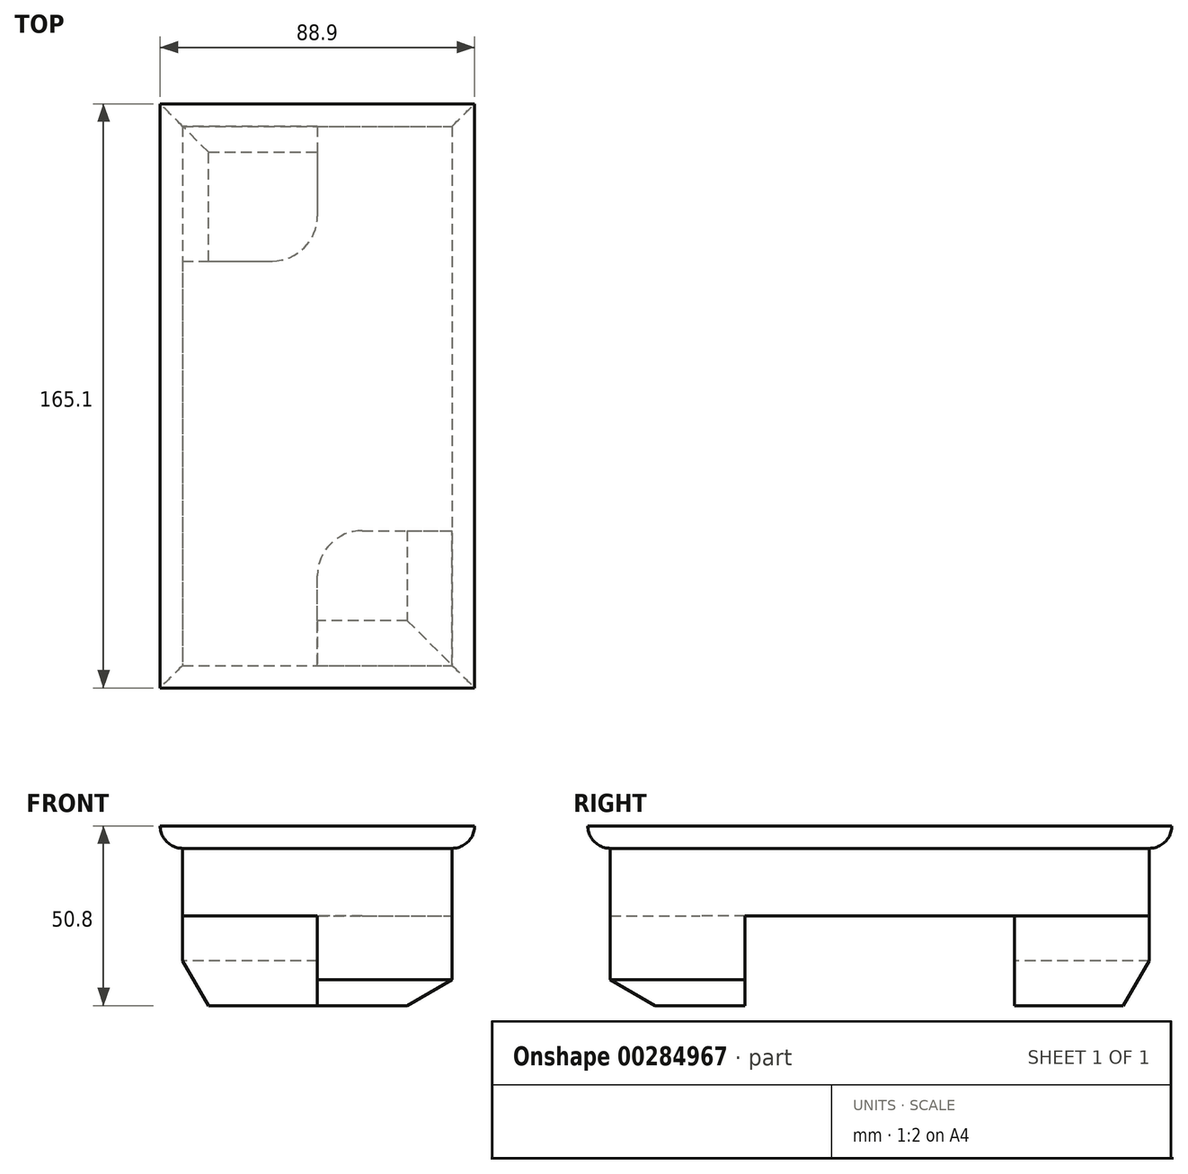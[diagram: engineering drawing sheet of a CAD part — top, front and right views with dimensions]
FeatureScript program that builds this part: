
annotation { "Feature Type Name" : "Feature", "Feature Type Description" : "" }
export const myFeature = defineFeature(function(context is Context, id is Id, definition is map)
    precondition{}
    {
        {
            var Q0;
            Q0=qCreatedBy(makeId("Top.planeOp"),FACE);
            var sketch = newSketch(context, id + "F0", { "sketchPlane" : qUnion([Q0])});
            skLineSegment(sketch, "E0.bottom", {"start": v(-82.55, 51.12) * mm, "end": v(-6.35, 51.12) * mm});
            skLineSegment(sketch, "E0.top", {"start": v(-82.55, -101.28) * mm, "end": v(-6.35, -101.28) * mm});
            skLineSegment(sketch, "E0.left", {"start": v(-82.55, 51.12) * mm, "end": v(-82.55, -101.28) * mm});
            skLineSegment(sketch, "E0.right", {"start": v(-6.35, 51.12) * mm, "end": v(-6.35, -101.28) * mm});
            skLineSegment(sketch, "E1.0", {"start": v(-88.9, 57.47) * mm, "end": v(0, 57.47) * mm});
            skLineSegment(sketch, "E1.1", {"start": v(-88.9, 57.47) * mm, "end": v(-88.9, -107.63) * mm});
            skLineSegment(sketch, "E1.2", {"start": v(-88.9, -107.63) * mm, "end": v(0, -107.63) * mm});
            skLineSegment(sketch, "E1.3", {"start": v(0, 57.47) * mm, "end": v(0, -107.63) * mm});
            skLineSegment(sketch, "E2", {"start": v(-82.55, 13.02) * mm, "end": v(-57.15, 13.02) * mm});
            skLineSegment(sketch, "E3", {"start": v(-44.45, 51.12) * mm, "end": v(-44.45, 25.72) * mm});
            skLineSegment(sketch, "E4", {"start": v(-44.45, -101.28) * mm, "end": v(-44.45, -75.88) * mm});
            skLineSegment(sketch, "E5", {"start": v(-31.75, -63.18) * mm, "end": v(-6.35, -63.18) * mm});
            skPoint(sketch, "E6.visualSharp", {"position": v(-44.45, 13.02) * mm});
            skArc(sketch, "E6.filletArc", {"start": v(-57.15, 13.02) * mm, "mid": v(-48.17, 16.74) * mm, "end": v(-44.45, 25.72) * mm});
            skPoint(sketch, "E7.visualSharp", {"position": v(-44.45, -63.18) * mm});
            skArc(sketch, "E7.filletArc", {"start": v(-31.75, -63.18) * mm, "mid": v(-40.73, -66.9) * mm, "end": v(-44.45, -75.88) * mm});
            skSolve(sketch);
        }
        {
            var Q0;
            Q0=makeQuery(id+"F0.imprint","IMPRINT",FACE,{"disambiguationData":[TD([[makeQuery(id+"F0.imprint","IMPRINT",EDGE,{"derivedFrom":sQuery(id+"F0.wireOp",EDGE,"E1.0")}),-1.0]])]});
            var Q1;
            {var subQ3=sQuery(id+"F0.wireOp",EDGE,"E2");Q1=makeQuery(id+"F0.imprint","IMPRINT",FACE,{"disambiguationData":[TD([[makeQuery(id+"F0.imprint","IMPRINT",EDGE,{"derivedFrom":subQ3}),-1.0]])]});}
            var Q2;
            {var subQ1=sQuery(id+"F0.wireOp",EDGE,"E4");Q2=makeQuery(id+"F0.imprint","IMPRINT",FACE,{"disambiguationData":[TD([[makeQuery(id+"F0.imprint","IMPRINT",EDGE,{"derivedFrom":subQ1}),-1.0]])]});}
            var Q3;
            {var subQ1=sQuery(id+"F0.wireOp",EDGE,"E2");Q3=makeQuery(id+"F0.imprint","IMPRINT",FACE,{"disambiguationData":[TD([[makeQuery(id+"F0.imprint","IMPRINT",EDGE,{"derivedFrom":subQ1}),1.0]])]});}
            extrude(context, id + "F1", {"entities" : qUnion([Q0, Q1, Q2, Q3]), "oppositeDirection" : true, "depth" : 6.35 * mm});
        }
        {
            var Q0;
            {var subQ3=sQuery(id+"F0.wireOp",EDGE,"E2");Q0=makeQuery(id+"F0.imprint","IMPRINT",FACE,{"disambiguationData":[TD([[makeQuery(id+"F0.imprint","IMPRINT",EDGE,{"derivedFrom":subQ3}),-1.0]])]});}
            extrude(context, id + "F2", {"entities" : qUnion([Q0]), "operationType" : NewBodyOperationType.ADD, "oppositeDirection" : true, "depth" : 25.4 * mm});
        }
        {
            var Q0;
            {var subQ1=sQuery(id+"F0.wireOp",EDGE,"E4");Q0=makeQuery(id+"F0.imprint","IMPRINT",FACE,{"disambiguationData":[TD([[makeQuery(id+"F0.imprint","IMPRINT",EDGE,{"derivedFrom":subQ1}),-1.0]])]});}
            var Q1;
            {var subQ1=sQuery(id+"F0.wireOp",EDGE,"E2");Q1=makeQuery(id+"F0.imprint","IMPRINT",FACE,{"disambiguationData":[TD([[makeQuery(id+"F0.imprint","IMPRINT",EDGE,{"derivedFrom":subQ1}),1.0]])]});}
            extrude(context, id + "F3", {"entities" : qUnion([Q0, Q1]), "operationType" : NewBodyOperationType.ADD, "oppositeDirection" : true, "depth" : 50.8 * mm});
        }
        {
            var Q0;
            Q0=makeQuery(id+"F1.opExtrude","CAP_EDGE",EDGE,{"disambiguationData":[OSD([sQuery(id+"F0.wireOp",EDGE,"E1.0")])],"isStart":false});
            var Q1;
            Q1=makeQuery(id+"F1.opExtrude","CAP_EDGE",EDGE,{"disambiguationData":[OSD([sQuery(id+"F0.wireOp",EDGE,"E1.3")])],"isStart":false});
            var Q2;
            Q2=makeQuery(id+"F1.opExtrude","CAP_EDGE",EDGE,{"disambiguationData":[OSD([sQuery(id+"F0.wireOp",EDGE,"E1.2")])],"isStart":false});
            var Q3;
            Q3=makeQuery(id+"F1.opExtrude","CAP_EDGE",EDGE,{"disambiguationData":[OSD([sQuery(id+"F0.wireOp",EDGE,"E1.1")])],"isStart":false});
            fillet(context, id + "F4", {"entities" : qUnion([Q0, Q1, Q2, Q3]), "radius" : 6.35 * mm, "tangentPropagation" : true, "allowEdgeOverflow" : false});
        }
        {
            var Q0;
            Q0=makeQuery(id+"F3.opExtrude","CAP_EDGE",EDGE,{"disambiguationData":[OSD([sQuery(id+"F0.wireOp",EDGE,"E0.right")])],"isStart":false});
            var Q1;
            Q1=makeQuery(id+"F3.opExtrude","CAP_EDGE",EDGE,{"disambiguationData":[OSD([sQuery(id+"F0.wireOp",EDGE,"E0.top")])],"isStart":false});
            chamfer(context, id + "F5", {"entities" : qUnion([Q0, Q1]), "chamferType" : ChamferType.OFFSET_ANGLE, "width" : 12.7 * mm, "oppositeDirection" : false, "angle" : 30 * degree, "tangentPropagation" : true});
        }
        {
            var Q0;
            Q0=makeQuery(id+"F3.opExtrude","CAP_EDGE",EDGE,{"disambiguationData":[OSD([sQuery(id+"F0.wireOp",EDGE,"E0.left")])],"isStart":false});
            var Q1;
            Q1=makeQuery(id+"F3.opExtrude","CAP_EDGE",EDGE,{"disambiguationData":[OSD([sQuery(id+"F0.wireOp",EDGE,"E0.bottom")])],"isStart":false});
            chamfer(context, id + "F6", {"entities" : qUnion([Q0, Q1]), "chamferType" : ChamferType.OFFSET_ANGLE, "width" : 12.7 * mm, "oppositeDirection" : false, "angle" : 30 * degree, "tangentPropagation" : true});
        }
    });
